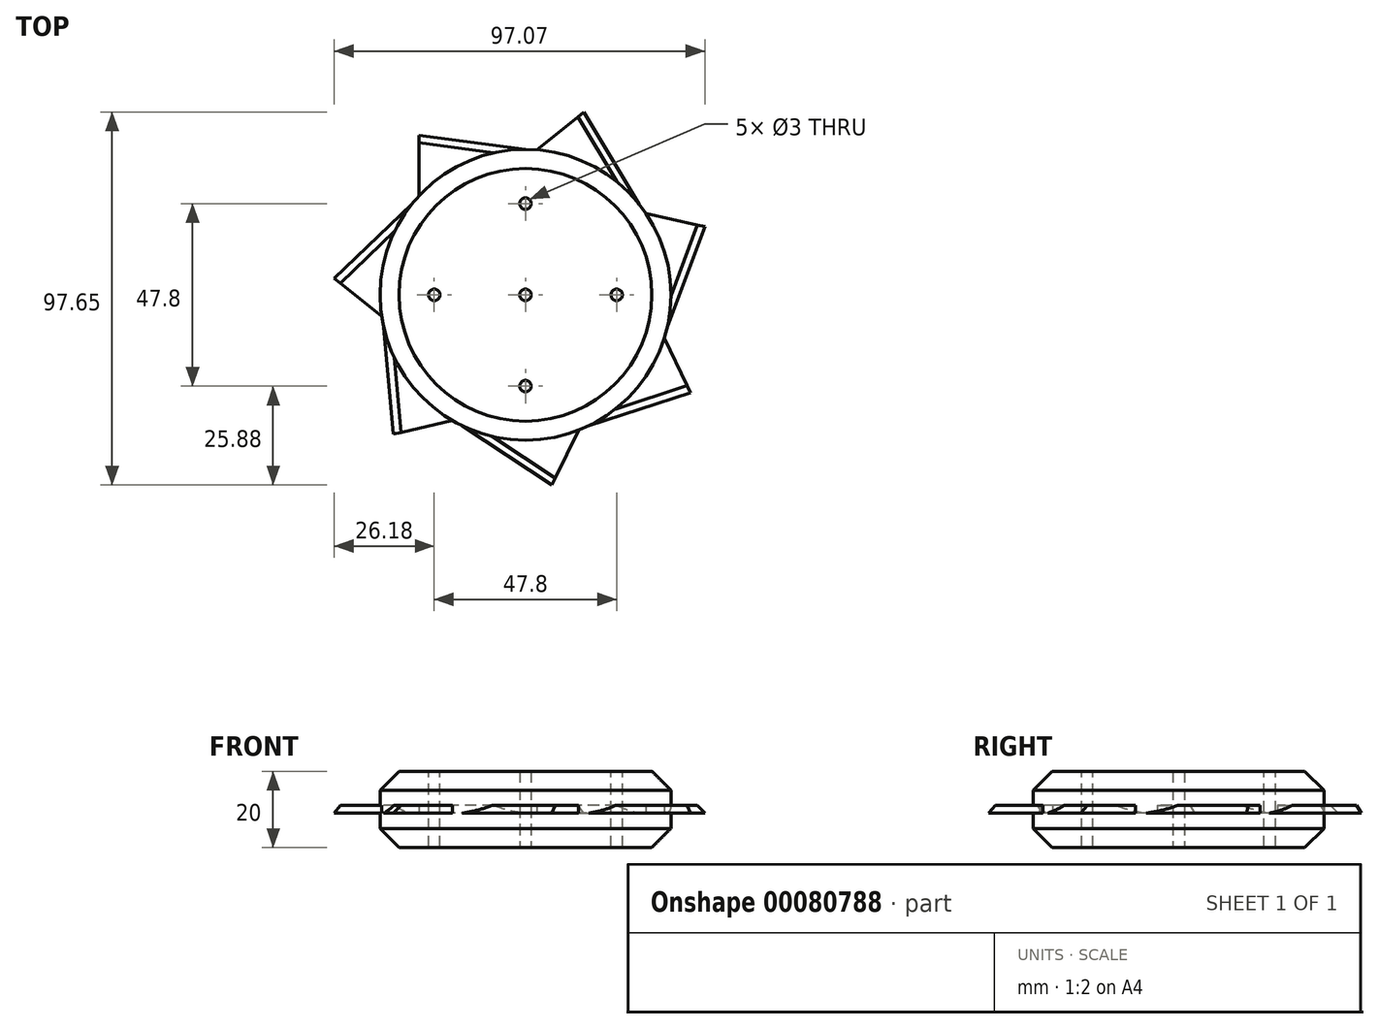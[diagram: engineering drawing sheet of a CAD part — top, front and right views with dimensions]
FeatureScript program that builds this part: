
annotation { "Feature Type Name" : "Feature", "Feature Type Description" : "" }
export const myFeature = defineFeature(function(context is Context, id is Id, definition is map)
    precondition{}
    {
        {
            var Q0;
            Q0=qCreatedBy(makeId("Top.planeOp"),FACE);
            var sketch = newSketch(context, id + "F0", { "sketchPlane" : qUnion([Q0])});
            skCircle(sketch, "E0", {"center": v(0, 0) * mm, "radius": 38.1 * mm});
            skLineSegment(sketch, "E1", {"start": v(-27.86, 25.98) * mm, "end": v(-27.86, 41.84) * mm});
            skLineSegment(sketch, "E2", {"start": v(-27.86, 41.84) * mm, "end": v(0, 38.1) * mm});
            skCircle(sketch, "E3", {"center": v(0, 0) * mm, "radius": 1.5 * mm});
            skLineSegment(sketch, "E4.1.0", {"start": v(-50.08, 4.3) * mm, "end": v(-29.79, 23.75) * mm});
            skLineSegment(sketch, "E4.1.1", {"start": v(-37.69, -5.58) * mm, "end": v(-50.08, 4.3) * mm});
            skLineSegment(sketch, "E4.2.0", {"start": v(-34.59, -36.48) * mm, "end": v(-37.14, -8.48) * mm});
            skLineSegment(sketch, "E4.2.1", {"start": v(-19.13, -32.95) * mm, "end": v(-34.59, -36.48) * mm});
            skLineSegment(sketch, "E4.3.0", {"start": v(6.95, -49.78) * mm, "end": v(-16.53, -34.33) * mm});
            skLineSegment(sketch, "E4.3.1", {"start": v(13.83, -35.5) * mm, "end": v(6.95, -49.78) * mm});
            skLineSegment(sketch, "E4.4.0", {"start": v(43.26, -25.6) * mm, "end": v(16.53, -34.33) * mm});
            skLineSegment(sketch, "E4.4.1", {"start": v(36.38, -11.32) * mm, "end": v(43.26, -25.6) * mm});
            skLineSegment(sketch, "E4.5.0", {"start": v(46.99, 17.86) * mm, "end": v(37.14, -8.48) * mm});
            skLineSegment(sketch, "E4.5.1", {"start": v(31.53, 21.38) * mm, "end": v(46.99, 17.86) * mm});
            skLineSegment(sketch, "E4.6.0", {"start": v(15.34, 47.87) * mm, "end": v(29.79, 23.75) * mm});
            skLineSegment(sketch, "E4.6.1", {"start": v(2.94, 37.99) * mm, "end": v(15.34, 47.87) * mm});
            skSolve(sketch);
        }
        {
            var Q0;
            Q0=makeQuery(id+"F0.imprint","IMPRINT",FACE,{"disambiguationData":[TD([[makeQuery(id+"F0.imprint","IMPRINT",EDGE,{"derivedFrom":sQuery(id+"F0.wireOp",EDGE,"E3")}),-1.0]])]});
            extrude(context, id + "F1", {"entities" : qUnion([Q0]), "depth" : 20 * mm, "symmetric" : true});
        }
        {
            var Q0;
            {var subQ0=sQuery(id+"F0.wireOp",EDGE,"E1");Q0=makeQuery(id+"F0.imprint","IMPRINT",FACE,{"disambiguationData":[TD([[makeQuery(id+"F0.imprint","IMPRINT",EDGE,{"derivedFrom":subQ0}),-1.0]])]});}
            var Q1;
            {var subQ0=sQuery(id+"F0.wireOp",EDGE,"13a3d45c-4b33-47fc-b7c6-be3670e8b462.7.0");Q1=makeQuery(id+"F0.imprint","IMPRINT",FACE,{"disambiguationData":[TD([[makeQuery(id+"F0.imprint","IMPRINT",EDGE,{"derivedFrom":subQ0}),-1.0]])]});}
            var Q2;
            {var subQ0=sQuery(id+"F0.wireOp",EDGE,"13a3d45c-4b33-47fc-b7c6-be3670e8b462.6.0");Q2=makeQuery(id+"F0.imprint","IMPRINT",FACE,{"disambiguationData":[TD([[makeQuery(id+"F0.imprint","IMPRINT",EDGE,{"derivedFrom":subQ0}),-1.0]])]});}
            var Q3;
            {var subQ0=sQuery(id+"F0.wireOp",EDGE,"13a3d45c-4b33-47fc-b7c6-be3670e8b462.5.0");Q3=makeQuery(id+"F0.imprint","IMPRINT",FACE,{"disambiguationData":[TD([[makeQuery(id+"F0.imprint","IMPRINT",EDGE,{"derivedFrom":subQ0}),-1.0]])]});}
            var Q4;
            {var subQ0=sQuery(id+"F0.wireOp",EDGE,"13a3d45c-4b33-47fc-b7c6-be3670e8b462.4.0");Q4=makeQuery(id+"F0.imprint","IMPRINT",FACE,{"disambiguationData":[TD([[makeQuery(id+"F0.imprint","IMPRINT",EDGE,{"derivedFrom":subQ0}),-1.0]])]});}
            var Q5;
            {var subQ0=sQuery(id+"F0.wireOp",EDGE,"13a3d45c-4b33-47fc-b7c6-be3670e8b462.3.0");Q5=makeQuery(id+"F0.imprint","IMPRINT",FACE,{"disambiguationData":[TD([[makeQuery(id+"F0.imprint","IMPRINT",EDGE,{"derivedFrom":subQ0}),-1.0]])]});}
            var Q6;
            {var subQ0=sQuery(id+"F0.wireOp",EDGE,"13a3d45c-4b33-47fc-b7c6-be3670e8b462.2.0");Q6=makeQuery(id+"F0.imprint","IMPRINT",FACE,{"disambiguationData":[TD([[makeQuery(id+"F0.imprint","IMPRINT",EDGE,{"derivedFrom":subQ0}),-1.0]])]});}
            var Q7;
            {var subQ0=sQuery(id+"F0.wireOp",EDGE,"13a3d45c-4b33-47fc-b7c6-be3670e8b462.1.0");Q7=makeQuery(id+"F0.imprint","IMPRINT",FACE,{"disambiguationData":[TD([[makeQuery(id+"F0.imprint","IMPRINT",EDGE,{"derivedFrom":subQ0}),-1.0]])]});}
            var Q8;
            {var subQ0=sQuery(id+"F0.wireOp",EDGE,"E4.6.0");Q8=makeQuery(id+"F0.imprint","IMPRINT",FACE,{"disambiguationData":[TD([[makeQuery(id+"F0.imprint","IMPRINT",EDGE,{"derivedFrom":subQ0}),-1.0]])]});}
            var Q9;
            {var subQ0=sQuery(id+"F0.wireOp",EDGE,"E4.5.0");Q9=makeQuery(id+"F0.imprint","IMPRINT",FACE,{"disambiguationData":[TD([[makeQuery(id+"F0.imprint","IMPRINT",EDGE,{"derivedFrom":subQ0}),-1.0]])]});}
            var Q10;
            {var subQ0=sQuery(id+"F0.wireOp",EDGE,"E4.4.0");Q10=makeQuery(id+"F0.imprint","IMPRINT",FACE,{"disambiguationData":[TD([[makeQuery(id+"F0.imprint","IMPRINT",EDGE,{"derivedFrom":subQ0}),-1.0]])]});}
            var Q11;
            {var subQ0=sQuery(id+"F0.wireOp",EDGE,"E4.3.0");Q11=makeQuery(id+"F0.imprint","IMPRINT",FACE,{"disambiguationData":[TD([[makeQuery(id+"F0.imprint","IMPRINT",EDGE,{"derivedFrom":subQ0}),-1.0]])]});}
            var Q12;
            {var subQ0=sQuery(id+"F0.wireOp",EDGE,"E4.2.0");Q12=makeQuery(id+"F0.imprint","IMPRINT",FACE,{"disambiguationData":[TD([[makeQuery(id+"F0.imprint","IMPRINT",EDGE,{"derivedFrom":subQ0}),-1.0]])]});}
            var Q13;
            {var subQ0=sQuery(id+"F0.wireOp",EDGE,"E4.1.0");Q13=makeQuery(id+"F0.imprint","IMPRINT",FACE,{"disambiguationData":[TD([[makeQuery(id+"F0.imprint","IMPRINT",EDGE,{"derivedFrom":subQ0}),-1.0]])]});}
            extrude(context, id + "F2", {"entities" : qUnion([Q0, Q1, Q2, Q3, Q4, Q5, Q6, Q7, Q8, Q9, Q10, Q11, Q12, Q13]), "operationType" : NewBodyOperationType.ADD, "depth" : 2 * mm, "symmetric" : true});
        }
        {
            var Q0;
            Q0=makeQuery(id+"F1.opExtrude","CAP_EDGE",EDGE,{"disambiguationData":[OSD([sQuery(id+"F0.wireOp",EDGE,"E0")])],"isStart":false});
            var Q1;
            Q1=makeQuery(id+"F1.opExtrude","CAP_EDGE",EDGE,{"disambiguationData":[OSD([sQuery(id+"F0.wireOp",EDGE,"E0")])],"isStart":true});
            chamfer(context, id + "F3", {"entities" : qUnion([Q0, Q1]), "width" : 5 * mm, "tangentPropagation" : true});
        }
        {
            var Q0;
            Q0=makeQuery(id+"F2.opExtrude","CAP_EDGE",EDGE,{"disambiguationData":[OSD([sQuery(id+"F0.wireOp",EDGE,"E4.3.0")])],"isStart":false});
            var Q1;
            Q1=makeQuery(id+"F2.opExtrude","CAP_EDGE",EDGE,{"disambiguationData":[OSD([sQuery(id+"F0.wireOp",EDGE,"E4.2.0")])],"isStart":false});
            var Q2;
            Q2=makeQuery(id+"F2.opExtrude","CAP_EDGE",EDGE,{"disambiguationData":[OSD([sQuery(id+"F0.wireOp",EDGE,"E4.4.0")])],"isStart":false});
            var Q3;
            Q3=makeQuery(id+"F2.opExtrude","CAP_EDGE",EDGE,{"disambiguationData":[OSD([sQuery(id+"F0.wireOp",EDGE,"E4.1.0")])],"isStart":false});
            var Q4;
            Q4=makeQuery(id+"F2.opExtrude","CAP_EDGE",EDGE,{"disambiguationData":[OSD([sQuery(id+"F0.wireOp",EDGE,"E2")])],"isStart":false});
            var Q5;
            Q5=makeQuery(id+"F2.opExtrude","CAP_EDGE",EDGE,{"disambiguationData":[OSD([sQuery(id+"F0.wireOp",EDGE,"E4.5.0")])],"isStart":false});
            var Q6;
            Q6=makeQuery(id+"F2.opExtrude","CAP_EDGE",EDGE,{"disambiguationData":[OSD([sQuery(id+"F0.wireOp",EDGE,"E4.6.0")])],"isStart":false});
            chamfer(context, id + "F4", {"entities" : qUnion([Q0, Q1, Q2, Q3, Q4, Q5, Q6]), "width" : 2 * mm, "tangentPropagation" : true});
        }
        {
            var Q0;
            Q0=makeQuery(id+"F1.opExtrude","CAP_FACE",FACE,{"disambiguationData":[OSD([sQuery(id+"F0.wireOp",EDGE,"E0"),sQuery(id+"F0.wireOp",EDGE,"E3")])],"isStart":false});
            var sketch = newSketch(context, id + "F5", { "sketchPlane" : qUnion([Q0])});
            skCircle(sketch, "E5", {"center": v(23.9, 0) * mm, "radius": 1.5 * mm});
            skCircle(sketch, "E6.1.0", {"center": v(0, 23.9) * mm, "radius": 1.5 * mm});
            skCircle(sketch, "E6.2.0", {"center": v(-23.9, 0) * mm, "radius": 1.5 * mm});
            skCircle(sketch, "E6.3.0", {"center": v(0, -23.9) * mm, "radius": 1.5 * mm});
            skPoint(sketch, "E6.center", {"position": v(0, 0) * mm});
            skSolve(sketch);
        }
        {
            var Q0;
            Q0=makeQuery(id+"F5.imprint","IMPRINT",FACE,{"disambiguationData":[TD([[makeQuery(id+"F5.imprint","IMPRINT",EDGE,{"derivedFrom":sQuery(id+"F5.wireOp",EDGE,"E6.2.0")}),1.0]])]});
            var Q1;
            Q1=makeQuery(id+"F5.imprint","IMPRINT",FACE,{"disambiguationData":[TD([[makeQuery(id+"F5.imprint","IMPRINT",EDGE,{"derivedFrom":sQuery(id+"F5.wireOp",EDGE,"E6.1.0")}),1.0]])]});
            var Q2;
            Q2=makeQuery(id+"F5.imprint","IMPRINT",FACE,{"disambiguationData":[TD([[makeQuery(id+"F5.imprint","IMPRINT",EDGE,{"derivedFrom":sQuery(id+"F5.wireOp",EDGE,"E5")}),1.0]])]});
            var Q3;
            Q3=makeQuery(id+"F5.imprint","IMPRINT",FACE,{"disambiguationData":[TD([[makeQuery(id+"F5.imprint","IMPRINT",EDGE,{"derivedFrom":sQuery(id+"F5.wireOp",EDGE,"E6.3.0")}),1.0]])]});
            extrude(context, id + "F6", {"entities" : qUnion([Q0, Q1, Q2, Q3]), "operationType" : NewBodyOperationType.REMOVE, "oppositeDirection" : true, "depth" : 50 * mm});
        }
    });
